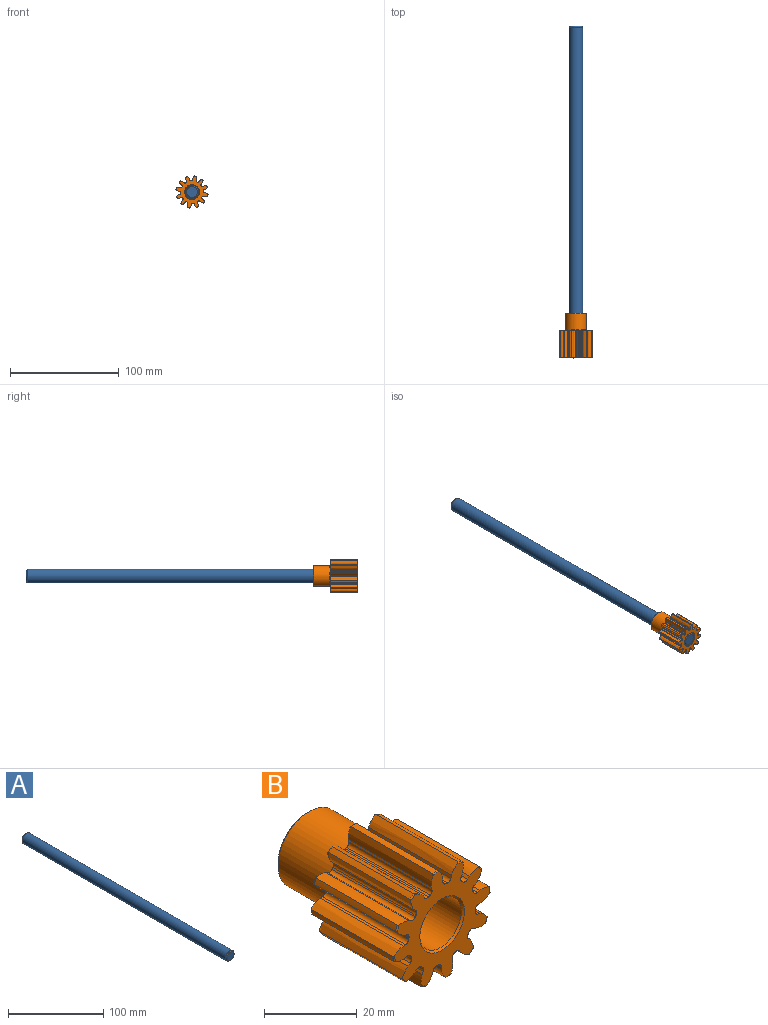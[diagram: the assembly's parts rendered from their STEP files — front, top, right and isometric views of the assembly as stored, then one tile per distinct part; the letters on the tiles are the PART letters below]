
ASSEMBLY  parts=2 mates=1
PART A: 5 faces, bbox 12.7x304.8x12.7 mm
  f0: cylinder r=6.35mm len=302.26mm, axis (0,1,0), area 12059.6mm2, adj f3,f4
  f1: plane 10.16x10.16mm, normal (0,-1,0), area 81.1mm2, adj f4
  f2: plane 10.16x10.16mm, normal (0,1,0), area 81.1mm2, adj f3
  f3: cone r=6.35mm half-angle=45deg, axis (0,-1,0), area 64.5mm2, adj f0,f2
  f4: cone r=5.08mm half-angle=45deg, axis (0,1,0), area 64.5mm2, adj f0,f1
PART B: 129 faces, bbox 29.7x41.1x29.7 mm
  f0: cylinder r=14.86mm len=24.81mm, axis (0,-1,0), area 36.2mm2, adj f1,f2,f115,f118
  f1: torus R=14.56mm, axis (0,-1,0), area 0.7mm2, adj f0,f33,f115,f118
  f2: torus R=14.56mm, axis (0,-1,0), area 0.7mm2, adj f0,f35,f115,f118
  f3: cylinder r=14.86mm len=24.81mm, axis (0,-1,0), area 36.2mm2, adj f4,f5,f108,f111
  f4: torus R=14.56mm, axis (0,-1,0), area 0.7mm2, adj f3,f33,f108,f111
  f5: torus R=14.56mm, axis (0,-1,0), area 0.7mm2, adj f3,f35,f108,f111
  f6: cylinder r=14.86mm len=24.81mm, axis (0,-1,0), area 36.2mm2, adj f7,f8,f101,f104
  f7: torus R=14.56mm, axis (0,-1,0), area 0.7mm2, adj f6,f33,f101,f104
  f8: torus R=14.56mm, axis (0,-1,0), area 0.7mm2, adj f6,f35,f101,f104
  f9: cylinder r=14.86mm len=24.81mm, axis (0,-1,0), area 36.2mm2, adj f10,f11,f94,f97
  f10: torus R=14.56mm, axis (0,-1,0), area 0.7mm2, adj f9,f33,f94,f97
  f11: torus R=14.56mm, axis (0,-1,0), area 0.7mm2, adj f9,f35,f94,f97
  f12: cylinder r=14.86mm len=24.81mm, axis (0,-1,0), area 36.2mm2, adj f13,f14,f87,f90
  f13: torus R=14.56mm, axis (0,-1,0), area 0.7mm2, adj f12,f33,f87,f90
  f14: torus R=14.56mm, axis (0,-1,0), area 0.7mm2, adj f12,f35,f87,f90
  f15: cylinder r=14.86mm len=24.81mm, axis (0,-1,0), area 36.2mm2, adj f16,f17,f80,f83
  f16: torus R=14.56mm, axis (0,-1,0), area 0.7mm2, adj f15,f33,f80,f83
  f17: torus R=14.56mm, axis (0,-1,0), area 0.7mm2, adj f15,f35,f80,f83
  f18: cylinder r=14.86mm len=24.81mm, axis (0,-1,0), area 36.2mm2, adj f19,f20,f73,f76
  f19: torus R=14.56mm, axis (0,-1,0), area 0.7mm2, adj f18,f33,f73,f76
  f20: torus R=14.56mm, axis (0,-1,0), area 0.7mm2, adj f18,f35,f73,f76
  f21: cylinder r=14.86mm len=24.81mm, axis (0,-1,0), area 36.2mm2, adj f22,f23,f66,f69
  f22: torus R=14.56mm, axis (0,-1,0), area 0.7mm2, adj f21,f33,f66,f69
  f23: torus R=14.56mm, axis (0,-1,0), area 0.7mm2, adj f21,f35,f66,f69
  f24: cylinder r=14.86mm len=24.81mm, axis (0,-1,0), area 36.2mm2, adj f25,f26,f59,f62
  f25: torus R=14.56mm, axis (0,-1,0), area 0.7mm2, adj f24,f33,f59,f62
  f26: torus R=14.56mm, axis (0,-1,0), area 0.7mm2, adj f24,f35,f59,f62
  f27: cylinder r=14.86mm len=24.81mm, axis (0,-1,0), area 36.2mm2, adj f28,f29,f52,f55
  f28: torus R=14.56mm, axis (0,-1,0), area 0.7mm2, adj f27,f33,f52,f55
  f29: torus R=14.56mm, axis (0,-1,0), area 0.7mm2, adj f27,f35,f52,f55
  f30: cylinder r=14.86mm len=24.81mm, axis (0,-1,0), area 36.2mm2, adj f31,f32,f44,f48
  f31: torus R=14.56mm, axis (0,-1,0), area 0.7mm2, adj f30,f33,f44,f48
  f32: torus R=14.56mm, axis (0,-1,0), area 0.7mm2, adj f30,f35,f44,f48
  f33: plane 29.18x29.18mm, normal (0,1,0), area 190.6mm2, adj f1,f4,f7,f10,f13,f16,f19,f22
  f34: cylinder r=14.86mm len=24.81mm, axis (0,-1,0), area 36.2mm2, adj f39,f40,f45,f122
  f35: plane 29.18x29.18mm, normal (0,-1,0), area 347.3mm2, adj f2,f5,f8,f11,f14,f17,f20,f23
  f36: cylinder r=9.53mm len=19.05mm, axis (0,-1,0), area 896.2mm2, adj f38,f128
  f37: plane 18.1x18.1mm, normal (0,1,0), area 110.8mm2, adj f126,f128
  f38: torus R=9.82mm, axis (0,-1,0), area 28.3mm2, adj f33,f36
  f39: torus R=14.56mm, axis (0,-1,0), area 0.7mm2, adj f33,f34,f45,f122
  f40: torus R=14.56mm, axis (0,-1,0), area 0.7mm2, adj f34,f35,f45,f122
  f41: plane 25.4x0.72mm, normal (-0.97,0,0.26), area 19mm2, adj f33,f35,f45,f46
  f42: cylinder r=10.25mm len=25.4mm, axis (0,-1,0), area 12.1mm2, adj f33,f35,f46,f47
  f43: plane 25.4x0.75mm, normal (1,0,0), area 19mm2, adj f33,f35,f44,f47
  f44: extruded ~25.4x2.88mm, area 82.4mm2, adj f30,f31,f32,f33,f35,f43
  f45: extruded ~25.4x2.41mm, area 82.4mm2, adj f33,f34,f35,f39,f40,f41
  f46: cylinder r=1mm len=25.4mm, axis (0,-1,0), area 37.1mm2, adj f33,f35,f41,f42
  f47: cylinder r=1mm len=25.4mm, axis (0,-1,0), area 37.1mm2, adj f33,f35,f42,f43
  f48: extruded ~25.4x3.15mm, area 82.4mm2, adj f30,f31,f32,f33,f35,f49
  f49: plane 25.4x0.72mm, normal (-0.97,0,-0.26), area 19mm2, adj f33,f35,f48,f50
  f50: cylinder r=1mm len=25.4mm, axis (0,-1,0), area 37.1mm2, adj f33,f35,f49,f51
  f51: cylinder r=10.25mm len=25.4mm, axis (0,-1,0), area 12.1mm2, adj f33,f35,f50,f54
  f52: extruded ~25.4x2.67mm, area 82.4mm2, adj f27,f28,f29,f33,f35,f53
  f53: plane 25.4x0.65mm, normal (0.87,0,0.5), area 19mm2, adj f33,f35,f52,f54
  f54: cylinder r=1mm len=25.4mm, axis (0,-1,0), area 37.1mm2, adj f33,f35,f51,f53
  f55: extruded ~25.4x3.04mm, area 82.4mm2, adj f27,f28,f29,f33,f35,f56
  f56: plane 25.4x0.53mm, normal (-0.71,0,-0.71), area 19mm2, adj f33,f35,f55,f57
  f57: cylinder r=1mm len=25.4mm, axis (0,-1,0), area 37.1mm2, adj f33,f35,f56,f58
  f58: cylinder r=10.25mm len=25.4mm, axis (0,-1,0), area 12.1mm2, adj f33,f35,f57,f61
  f59: extruded ~25.4x3.2mm, area 82.4mm2, adj f24,f25,f26,f33,f35,f60
  f60: plane 25.4x0.65mm, normal (0.5,0,0.87), area 19mm2, adj f33,f35,f59,f61
  f61: cylinder r=1mm len=25.4mm, axis (0,-1,0), area 37.1mm2, adj f33,f35,f58,f60
  f62: extruded ~25.4x2.41mm, area 82.4mm2, adj f24,f25,f26,f33,f35,f63
  f63: plane 25.4x0.72mm, normal (-0.26,0,-0.97), area 19mm2, adj f33,f35,f62,f64
  f64: cylinder r=1mm len=25.4mm, axis (0,-1,0), area 37.1mm2, adj f33,f35,f63,f65
  f65: cylinder r=10.25mm len=25.4mm, axis (0,-1,0), area 12.1mm2, adj f33,f35,f64,f68
  f66: extruded ~25.4x2.88mm, area 82.4mm2, adj f21,f22,f23,f33,f35,f67
  f67: plane 25.4x0.75mm, normal (0,0,1), area 19mm2, adj f33,f35,f66,f68
  f68: cylinder r=1mm len=25.4mm, axis (0,-1,0), area 37.1mm2, adj f33,f35,f65,f67
  f69: extruded ~25.4x3.15mm, area 82.4mm2, adj f21,f22,f23,f33,f35,f70
  f70: plane 25.4x0.72mm, normal (0.26,0,-0.97), area 19mm2, adj f33,f35,f69,f71
  f71: cylinder r=1mm len=25.4mm, axis (0,-1,0), area 37.1mm2, adj f33,f35,f70,f72
  f72: cylinder r=10.25mm len=25.4mm, axis (0,-1,0), area 12.1mm2, adj f33,f35,f71,f75
  f73: extruded ~25.4x2.67mm, area 82.4mm2, adj f18,f19,f20,f33,f35,f74
  f74: plane 25.4x0.65mm, normal (-0.5,0,0.87), area 19mm2, adj f33,f35,f73,f75
  f75: cylinder r=1mm len=25.4mm, axis (0,-1,0), area 37.1mm2, adj f33,f35,f72,f74
  f76: extruded ~25.4x3.04mm, area 82.4mm2, adj f18,f19,f20,f33,f35,f77
  f77: plane 25.4x0.53mm, normal (0.71,0,-0.71), area 19mm2, adj f33,f35,f76,f78
  f78: cylinder r=1mm len=25.4mm, axis (0,-1,0), area 37.1mm2, adj f33,f35,f77,f79
  f79: cylinder r=10.25mm len=25.4mm, axis (0,-1,0), area 12.1mm2, adj f33,f35,f78,f82
  f80: extruded ~25.4x3.2mm, area 82.4mm2, adj f15,f16,f17,f33,f35,f81
  f81: plane 25.4x0.65mm, normal (-0.87,0,0.5), area 19mm2, adj f33,f35,f80,f82
  f82: cylinder r=1mm len=25.4mm, axis (0,-1,0), area 37.1mm2, adj f33,f35,f79,f81
  f83: extruded ~25.4x2.41mm, area 82.4mm2, adj f15,f16,f17,f33,f35,f84
  f84: plane 25.4x0.72mm, normal (0.97,0,-0.26), area 19mm2, adj f33,f35,f83,f85
  f85: cylinder r=1mm len=25.4mm, axis (0,-1,0), area 37.1mm2, adj f33,f35,f84,f86
  f86: cylinder r=10.25mm len=25.4mm, axis (0,-1,0), area 12.1mm2, adj f33,f35,f85,f89
  f87: extruded ~25.4x2.88mm, area 82.4mm2, adj f12,f13,f14,f33,f35,f88
  f88: plane 25.4x0.75mm, normal (-1,0,0), area 19mm2, adj f33,f35,f87,f89
  f89: cylinder r=1mm len=25.4mm, axis (0,-1,0), area 37.1mm2, adj f33,f35,f86,f88
  f90: extruded ~25.4x3.15mm, area 82.4mm2, adj f12,f13,f14,f33,f35,f91
  f91: plane 25.4x0.72mm, normal (0.97,0,0.26), area 19mm2, adj f33,f35,f90,f92
  f92: cylinder r=1mm len=25.4mm, axis (0,-1,0), area 37.1mm2, adj f33,f35,f91,f93
  f93: cylinder r=10.25mm len=25.4mm, axis (0,-1,0), area 12.1mm2, adj f33,f35,f92,f96
  f94: extruded ~25.4x2.67mm, area 82.4mm2, adj f9,f10,f11,f33,f35,f95
  f95: plane 25.4x0.65mm, normal (-0.87,0,-0.5), area 19mm2, adj f33,f35,f94,f96
  f96: cylinder r=1mm len=25.4mm, axis (0,-1,0), area 37.1mm2, adj f33,f35,f93,f95
  f97: extruded ~25.4x3.04mm, area 82.4mm2, adj f9,f10,f11,f33,f35,f98
  f98: plane 25.4x0.53mm, normal (0.71,0,0.71), area 19mm2, adj f33,f35,f97,f99
  f99: cylinder r=1mm len=25.4mm, axis (0,-1,0), area 37.1mm2, adj f33,f35,f98,f100
  f100: cylinder r=10.25mm len=25.4mm, axis (0,-1,0), area 12.1mm2, adj f33,f35,f99,f103
  f101: extruded ~25.4x3.2mm, area 82.4mm2, adj f6,f7,f8,f33,f35,f102
  f102: plane 25.4x0.65mm, normal (-0.5,0,-0.87), area 19mm2, adj f33,f35,f101,f103
  f103: cylinder r=1mm len=25.4mm, axis (0,-1,0), area 37.1mm2, adj f33,f35,f100,f102
  f104: extruded ~25.4x2.41mm, area 82.4mm2, adj f6,f7,f8,f33,f35,f105
  f105: plane 25.4x0.72mm, normal (0.26,0,0.97), area 19mm2, adj f33,f35,f104,f106
  f106: cylinder r=1mm len=25.4mm, axis (0,-1,0), area 37.1mm2, adj f33,f35,f105,f107
  f107: cylinder r=10.25mm len=25.4mm, axis (0,-1,0), area 12.1mm2, adj f33,f35,f106,f110
  f108: extruded ~25.4x2.88mm, area 82.4mm2, adj f3,f4,f5,f33,f35,f109
  f109: plane 25.4x0.75mm, normal (0,0,-1), area 19mm2, adj f33,f35,f108,f110
  f110: cylinder r=1mm len=25.4mm, axis (0,-1,0), area 37.1mm2, adj f33,f35,f107,f109
  f111: extruded ~25.4x3.15mm, area 82.4mm2, adj f3,f4,f5,f33,f35,f112
  f112: plane 25.4x0.72mm, normal (-0.26,0,0.97), area 19mm2, adj f33,f35,f111,f113
  f113: cylinder r=1mm len=25.4mm, axis (0,-1,0), area 37.1mm2, adj f33,f35,f112,f114
  f114: cylinder r=10.25mm len=25.4mm, axis (0,-1,0), area 12.1mm2, adj f33,f35,f113,f117
  f115: extruded ~25.4x2.67mm, area 82.4mm2, adj f0,f1,f2,f33,f35,f116
  f116: plane 25.4x0.65mm, normal (0.5,0,-0.87), area 19mm2, adj f33,f35,f115,f117
  f117: cylinder r=1mm len=25.4mm, axis (0,-1,0), area 37.1mm2, adj f33,f35,f114,f116
  f118: extruded ~25.4x3.04mm, area 82.4mm2, adj f0,f1,f2,f33,f35,f119
  f119: plane 25.4x0.53mm, normal (-0.71,0,0.71), area 19mm2, adj f33,f35,f118,f120
  f120: cylinder r=1mm len=25.4mm, axis (0,-1,0), area 37.1mm2, adj f33,f35,f119,f121
  f121: cylinder r=10.25mm len=25.4mm, axis (0,-1,0), area 12.1mm2, adj f33,f35,f120,f124
  f122: extruded ~25.4x3.2mm, area 82.4mm2, adj f33,f34,f35,f39,f40,f123
  f123: plane 25.4x0.65mm, normal (0.87,0,-0.5), area 19mm2, adj f33,f35,f122,f124
  f124: cylinder r=1mm len=25.4mm, axis (0,-1,0), area 37.1mm2, adj f33,f35,f121,f123
  f125: cylinder r=6.35mm len=40.2mm, axis (0,-1,0), area 1603.7mm2, adj f126,f127
  f126: cone r=6.83mm half-angle=45deg, axis (0,1,0), area 27.9mm2, adj f37,f125
  f127: cone r=6.35mm half-angle=45deg, axis (0,-1,0), area 27.9mm2, adj f35,f125
  f128: cone r=9.53mm half-angle=45deg, axis (0,-1,0), area 39.3mm2, adj f36,f37
PLACE A t=(-21.1,111.96,-3.31)mm fixed
PLACE B rot(axis=(0,-1,0),11.3deg) t=(-21.1,-40.44,-3.31)mm
MATE revolute B.f0 <-> A.f0  axis (0,-1,0) through (-21.1,-40.44,-3.31)mm
